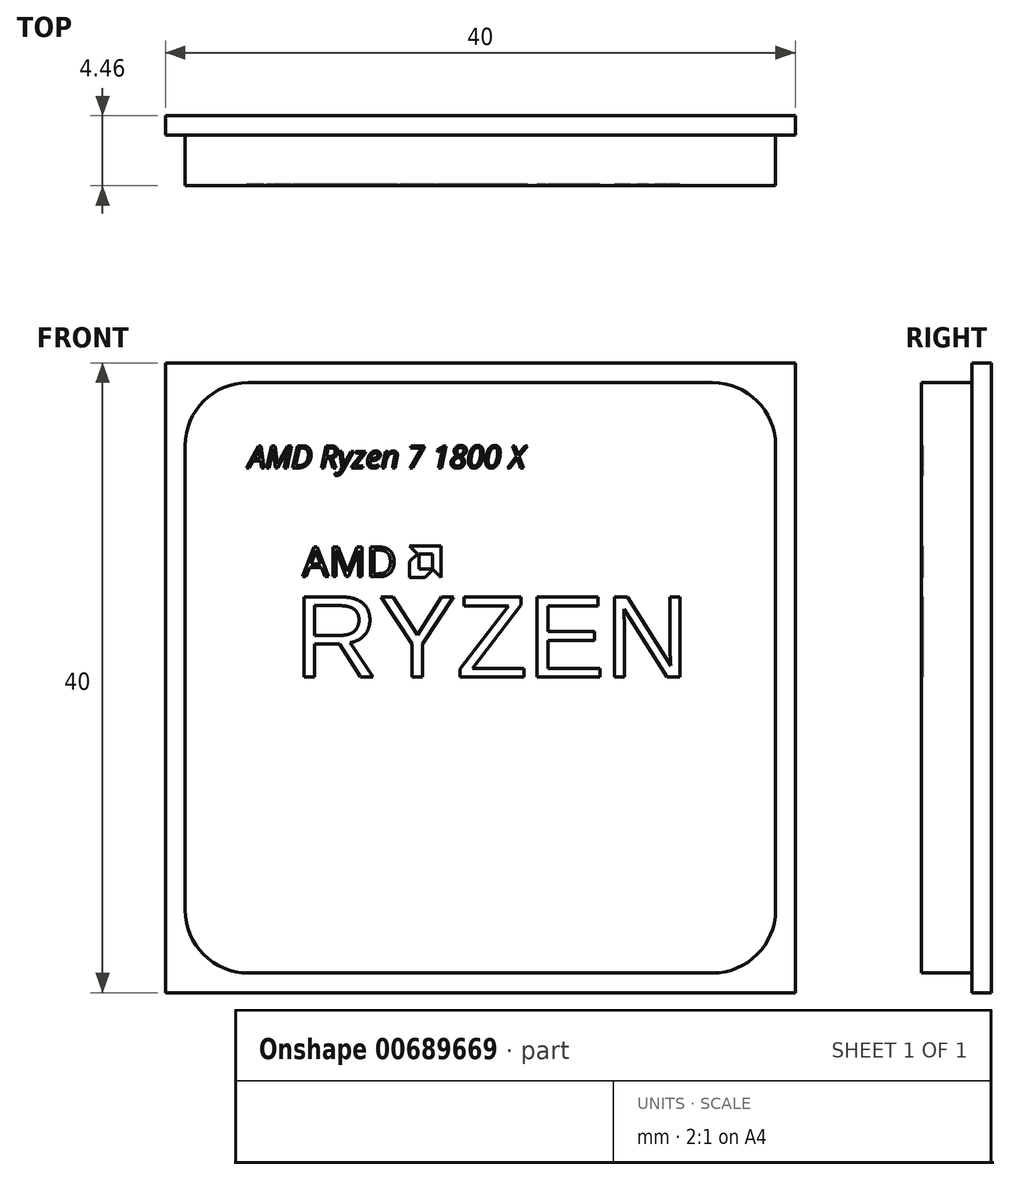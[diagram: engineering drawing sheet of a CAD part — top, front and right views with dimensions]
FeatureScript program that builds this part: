
annotation { "Feature Type Name" : "Feature", "Feature Type Description" : "" }
export const myFeature = defineFeature(function(context is Context, id is Id, definition is map)
    precondition{}
    {
        {
            var Q0;
            Q0=qCreatedBy(makeId("Front.planeOp"),FACE);
            var sketch = newSketch(context, id + "F0", { "sketchPlane" : qUnion([Q0])});
            skLineSegment(sketch, "E0.bottom", {"start": v(0, 40) * mm, "end": v(40, 40) * mm});
            skLineSegment(sketch, "E0.top", {"start": v(0, 0) * mm, "end": v(40, 0) * mm});
            skLineSegment(sketch, "E0.left", {"start": v(0, 40) * mm, "end": v(0, 0) * mm});
            skLineSegment(sketch, "E0.right", {"start": v(40, 40) * mm, "end": v(40, 0) * mm});
            skSolve(sketch);
        }
        {
            var Q0;
            Q0 = qSketchRegion(id + "F0", true);
            extrude(context, id + "F1", {"entities" : qUnion([Q0]), "depth" : 1.23 * mm, "offsetDistance" : 25 * mm});
        }
        {
            var Q0;
            Q0=makeQuery(id+"F1.opExtrude","CAP_FACE",FACE,{"disambiguationData":[OSD([sQuery(id+"F0.wireOp",EDGE,"E0.bottom"),sQuery(id+"F0.wireOp",EDGE,"E0.top"),sQuery(id+"F0.wireOp",EDGE,"E0.left"),sQuery(id+"F0.wireOp",EDGE,"E0.right")])],"isStart":false});
            var sketch = newSketch(context, id + "F2", { "sketchPlane" : qUnion([Q0])});
            skLineSegment(sketch, "E1.bottom", {"start": v(5.25, 38.75) * mm, "end": v(34.75, 38.75) * mm});
            skLineSegment(sketch, "E1.top", {"start": v(5.25, 1.25) * mm, "end": v(34.75, 1.25) * mm});
            skLineSegment(sketch, "E1.left", {"start": v(1.25, 34.75) * mm, "end": v(1.25, 5.25) * mm});
            skLineSegment(sketch, "E1.right", {"start": v(38.75, 34.75) * mm, "end": v(38.75, 5.25) * mm});
            skArc(sketch, "E2.filletArc", {"start": v(5.25, 38.75) * mm, "mid": v(2.42, 37.58) * mm, "end": v(1.25, 34.75) * mm});
            skArc(sketch, "E3.filletArc", {"start": v(38.75, 34.75) * mm, "mid": v(37.58, 37.58) * mm, "end": v(34.75, 38.75) * mm});
            skArc(sketch, "E4.filletArc", {"start": v(34.75, 1.25) * mm, "mid": v(37.58, 2.42) * mm, "end": v(38.75, 5.25) * mm});
            skArc(sketch, "E5.filletArc", {"start": v(1.25, 5.25) * mm, "mid": v(2.42, 2.42) * mm, "end": v(5.25, 1.25) * mm});
            skSolve(sketch);
        }
        {
            var Q0;
            Q0 = qSketchRegion(id + "F2", true);
            extrude(context, id + "F3", {"entities" : qUnion([Q0]), "operationType" : NewBodyOperationType.ADD, "depth" : 3.23 * mm, "offsetDistance" : 25 * mm});
        }
        {
            var Q0;
            Q0=makeQuery(id+"F3.opExtrude","CAP_FACE",FACE,{"disambiguationData":[OSD([sQuery(id+"F2.wireOp",EDGE,"E1.bottom"),sQuery(id+"F2.wireOp",EDGE,"E1.top"),sQuery(id+"F2.wireOp",EDGE,"E1.left"),sQuery(id+"F2.wireOp",EDGE,"E1.right"),sQuery(id+"F2.wireOp",EDGE,"E2.filletArc"),sQuery(id+"F2.wireOp",EDGE,"E3.filletArc"),sQuery(id+"F2.wireOp",EDGE,"E4.filletArc"),sQuery(id+"F2.wireOp",EDGE,"E5.filletArc")])],"isStart":false});
            var sketch = newSketch(context, id + "F4", { "sketchPlane" : qUnion([Q0])});
            skText(sketch, "E6", { "text": "AMD Ryzen 7 1800 X", "fontName": "OpenSans-Italic.ttf"});
            skText(sketch, "E7", { "text": "AMD", "fontName": "OpenSans-Regular.ttf"});
            skText(sketch, "E8", { "text": "RYZEN", "fontName": "Arimo-Regular.ttf"});
            skLineSegment(sketch, "E9.bottom", {"start": v(15.5, 28.38) * mm, "end": v(17.5, 28.38) * mm});
            skLineSegment(sketch, "E9.top", {"start": v(15.5, 26.38) * mm, "end": v(16.5, 26.38) * mm});
            skLineSegment(sketch, "E9.left", {"start": v(15.5, 27.38) * mm, "end": v(15.5, 26.38) * mm});
            skLineSegment(sketch, "E9.right", {"start": v(17.5, 28.38) * mm, "end": v(17.5, 26.38) * mm});
            skLineSegment(sketch, "E10", {"start": v(15.5, 28.38) * mm, "end": v(16, 27.88) * mm});
            skLineSegment(sketch, "E11", {"start": v(16, 27.88) * mm, "end": v(15.5, 27.38) * mm});
            skLineSegment(sketch, "E12", {"start": v(17, 26.88) * mm, "end": v(16.5, 26.38) * mm});
            skLineSegment(sketch, "E13.trimOffspring", {"start": v(17, 26.88) * mm, "end": v(17.5, 26.38) * mm});
            skLineSegment(sketch, "E14.bottom", {"start": v(16.09, 27.86) * mm, "end": v(16.96, 27.86) * mm});
            skLineSegment(sketch, "E14.top", {"start": v(16.09, 26.91) * mm, "end": v(16.96, 26.91) * mm});
            skLineSegment(sketch, "E14.left", {"start": v(16.09, 27.86) * mm, "end": v(16.09, 26.91) * mm});
            skLineSegment(sketch, "E14.right", {"start": v(16.96, 27.86) * mm, "end": v(16.96, 26.91) * mm});
            const initialGuessF4  = {"E6": [0.00525, 0.03333, 1, 0, 0.00142], "E7": [0.0087, 0.02642, 1, 0, 0.0019], "E8": [0.00818, 0.02004, 1, 0, 0.00533]};
            skSetInitialGuess(sketch, initialGuessF4);
            skSolve(sketch);
        }
        {
            var Q0;
            Q0 = qSketchRegion(id + "F4", true);
            extrude(context, id + "F5", {"entities" : qUnion([Q0]), "operationType" : NewBodyOperationType.REMOVE, "oppositeDirection" : true, "depth" : .1 * mm, "offsetDistance" : 25 * mm});
        }
    });
